# Revit family: HERZ Circuit chutoff valve 4218 AGF
name_source: partatom
category: Rohrzubehör
units: mm (PartAtom-declared; Revit-internal decimal feet)

## family parameters
Arbeitsebenenbasiert = Nein
Beim Laden mit Abzugskörper schneiden = Nein
Bemaßung runder Anschluss = Durchmesser verwenden
Gemeinsam genutzt = Nein
Immer vertikal = Ja
Teiletyp = Unterbricht

## types (1)
- HERZ Circuit chutoff valve 4218 AGF
    Application = For isolation in heating or cooling installations, risers, heat exchangers, heating and cooling systems.
    Hersteller = HERZ-Armaturen Ges.m.b.H.
    Max. operating pressure = 1600000.0 Pa
    Max. operating temperature from DN 40 = 110 °C
    Max. operating temperature up to DN 32 = 130 °C
    Medium = Heating water quality according ÖNORM H5195 or VDI-Standard 2035. The use of ethylene or propylene glycol in a
mixing ratio 25- 50% is allowed.
    O-rings = EPDM
    SCRNCODE = 05;11;2
    SCRNSEQ = ARM;ARM_TYP="ABSV";2
    URL = www.herzvalves.com
    Valve = upper part made of brass
    Valve body = cast iron GJL 250 according to EN 1561
    Vorgabe-Ansicht = 0 mm  [stored 0 ft]
    w = 10.00°

note: [stored X ft] marks values corroborated as IEEE doubles in the binary element streams (Revit-internal decimal feet)
